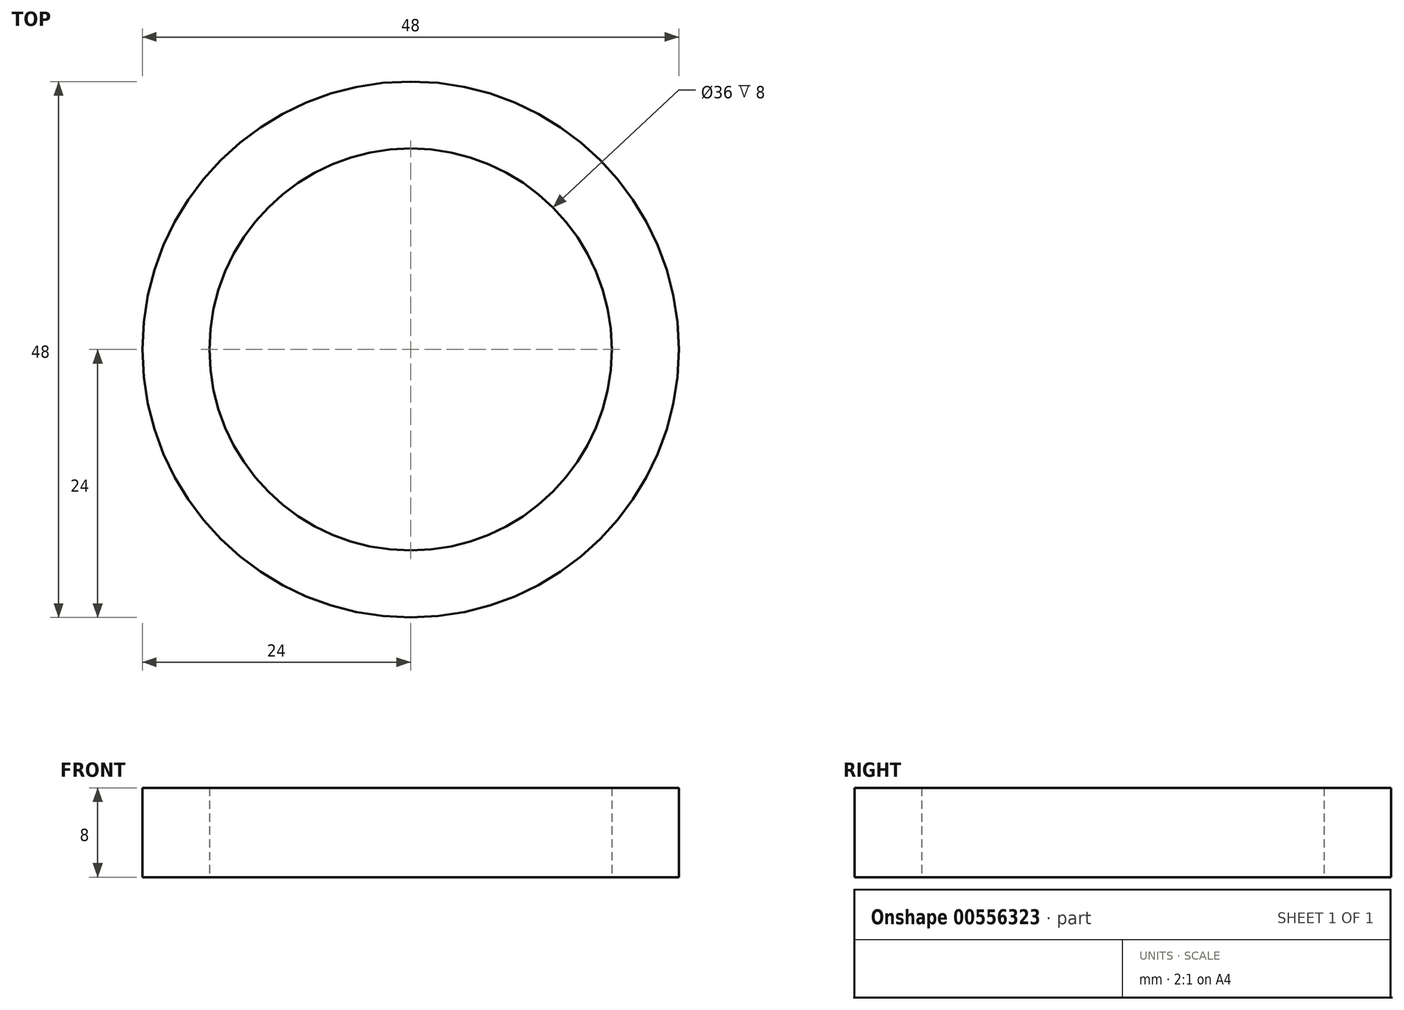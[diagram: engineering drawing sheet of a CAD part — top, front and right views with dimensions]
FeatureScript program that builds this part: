
annotation { "Feature Type Name" : "Feature", "Feature Type Description" : "" }
export const myFeature = defineFeature(function(context is Context, id is Id, definition is map)
    precondition{}
    {
        {
            var Q0;
            Q0=qCreatedBy(makeId("Top.planeOp"),FACE);
            var sketch = newSketch(context, id + "F0", { "sketchPlane" : qUnion([Q0])});
            skCircle(sketch, "E0", {"center": v(0, 0) * mm, "radius": 24 * mm});
            skCircle(sketch, "E1", {"center": v(0, 0) * mm, "radius": 18 * mm});
            skSolve(sketch);
        }
        {
            var Q0;
            Q0 = qSketchRegion(id + "F0", true);
            extrude(context, id + "F1", {"entities" : qUnion([Q0]), "depth" : 8 * mm, "offsetDistance" : 25 * mm});
        }
    });
